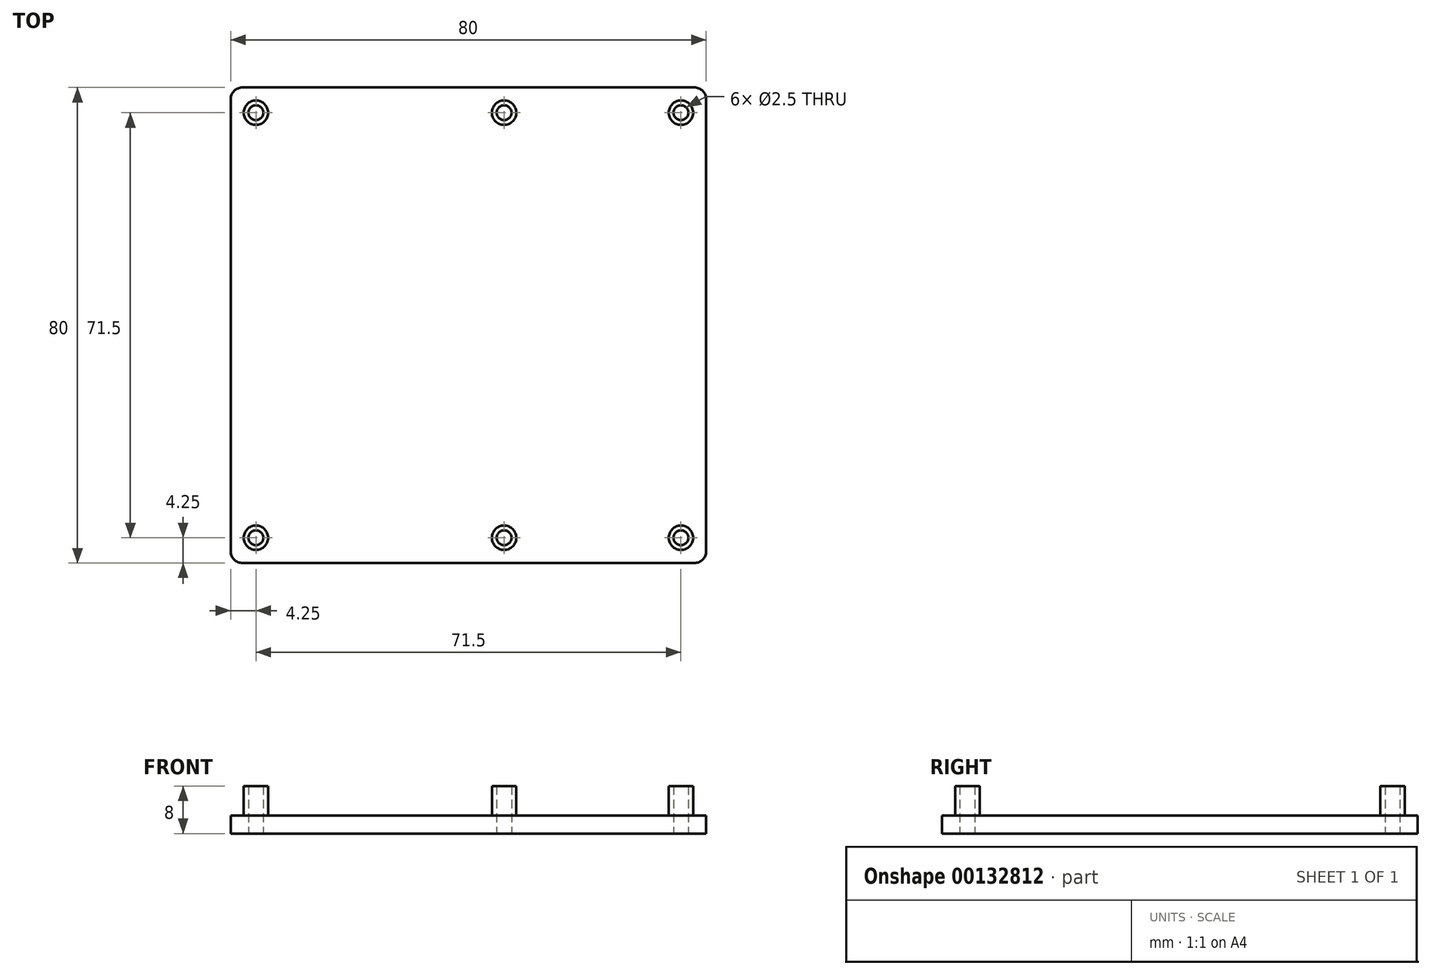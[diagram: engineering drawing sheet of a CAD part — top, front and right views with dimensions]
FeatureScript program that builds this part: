
annotation { "Feature Type Name" : "Feature", "Feature Type Description" : "" }
export const myFeature = defineFeature(function(context is Context, id is Id, definition is map)
    precondition{}
    {
        {
            var Q0;
            Q0=qCreatedBy(makeId("Top.planeOp"),FACE);
            var sketch = newSketch(context, id + "F0", { "sketchPlane" : qUnion([Q0])});
            skLineSegment(sketch, "E0.bottom", {"start": v(-38, 40) * mm, "end": v(38, 40) * mm});
            skLineSegment(sketch, "E0.top", {"start": v(-38, -40) * mm, "end": v(38, -40) * mm});
            skLineSegment(sketch, "E0.left", {"start": v(-40, 38) * mm, "end": v(-40, -38) * mm});
            skLineSegment(sketch, "E0.right", {"start": v(40, 38) * mm, "end": v(40, -38) * mm});
            skPoint(sketch, "E0.middle", {"position": v(0, 0) * mm});
            skPoint(sketch, "E1.visualSharp", {"position": v(-40, 40) * mm});
            skArc(sketch, "E1.filletArc", {"start": v(-38, 40) * mm, "mid": v(-39.41, 39.41) * mm, "end": v(-40, 38) * mm});
            skPoint(sketch, "E2.visualSharp", {"position": v(40, 40) * mm});
            skArc(sketch, "E2.filletArc", {"start": v(40, 38) * mm, "mid": v(39.41, 39.41) * mm, "end": v(38, 40) * mm});
            skPoint(sketch, "E3.visualSharp", {"position": v(40, -40) * mm});
            skArc(sketch, "E3.filletArc", {"start": v(38, -40) * mm, "mid": v(39.41, -39.41) * mm, "end": v(40, -38) * mm});
            skPoint(sketch, "E4.visualSharp", {"position": v(-40, -40) * mm});
            skArc(sketch, "E4.filletArc", {"start": v(-40, -38) * mm, "mid": v(-39.41, -39.41) * mm, "end": v(-38, -40) * mm});
            skSolve(sketch);
        }
        {
            var Q0;
            Q0=qCreatedBy(makeId("Top.planeOp"),FACE);
            var sketch = newSketch(context, id + "F1", { "sketchPlane" : qUnion([Q0])});
            skCircle(sketch, "E5", {"center": v(-35.75, 35.75) * mm, "radius": 2.05 * mm});
            skCircle(sketch, "E6", {"center": v(6, 35.75) * mm, "radius": 2.05 * mm});
            skCircle(sketch, "E7", {"center": v(35.75, 35.75) * mm, "radius": 2.05 * mm});
            skCircle(sketch, "E8", {"center": v(35.75, -35.75) * mm, "radius": 2.05 * mm});
            skCircle(sketch, "E9", {"center": v(6, -35.75) * mm, "radius": 2.05 * mm});
            skCircle(sketch, "E10", {"center": v(-35.75, -35.75) * mm, "radius": 2.05 * mm});
            skSolve(sketch);
        }
        {
            var Q0;
            Q0=qCreatedBy(makeId("Top.planeOp"),FACE);
            var sketch = newSketch(context, id + "F2", { "sketchPlane" : qUnion([Q0])});
            skCircle(sketch, "E11", {"center": v(-35.75, 35.75) * mm, "radius": 1.25 * mm});
            skCircle(sketch, "E12", {"center": v(6, 35.75) * mm, "radius": 1.25 * mm});
            skCircle(sketch, "E13", {"center": v(35.75, 35.75) * mm, "radius": 1.25 * mm});
            skCircle(sketch, "E14.MirrorC", {"center": v(35.75, -35.75) * mm, "radius": 1.25 * mm});
            skCircle(sketch, "E15.MirrorC", {"center": v(6, -35.75) * mm, "radius": 1.25 * mm});
            skCircle(sketch, "E16.MirrorC", {"center": v(-35.75, -35.75) * mm, "radius": 1.25 * mm});
            skSolve(sketch);
        }
        {
            var Q0;
            Q0 = qSketchRegion(id + "F0", true);
            extrude(context, id + "F3", {"entities" : qUnion([Q0]), "depth" : 3 * mm});
        }
        {
            var Q0;
            Q0 = qSketchRegion(id + "F1", true);
            extrude(context, id + "F4", {"entities" : qUnion([Q0]), "operationType" : NewBodyOperationType.ADD, "depth" : 8 * mm});
        }
        {
            var Q0;
            Q0 = qSketchRegion(id + "F2", true);
            extrude(context, id + "F5", {"entities" : qUnion([Q0]), "operationType" : NewBodyOperationType.REMOVE, "endBound" : BoundingType.THROUGH_ALL, "depth" : 25 * mm});
        }
    });
